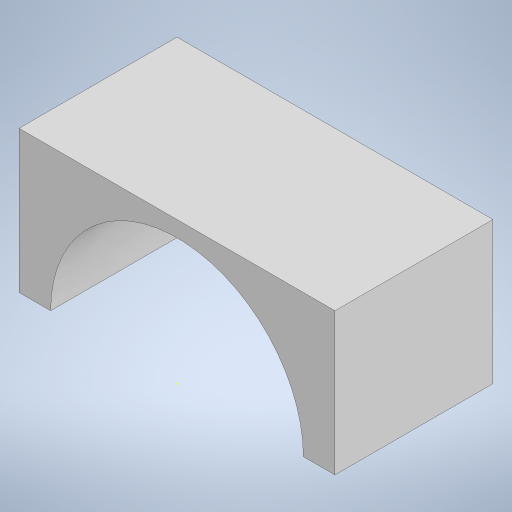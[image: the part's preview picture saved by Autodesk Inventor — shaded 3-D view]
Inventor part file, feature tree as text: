
AUTODESK INVENTOR PART (.ipt)
format: ipt  version: 2023 (Build 270158000, 158)  size: 200,704 bytes
history: native  units: mm
features: sketch x3, extrude x2
ambient origin geometry x8: Origin, YZ Plane, XZ Plane, XY Plane, X Axis, Y Axis, Z Axis, Center Point
bodies: Body1 (feature_tree)
feature tree (5):
  extrude  "Extrusion11"  Depth=45.0mm
  extrude  "Extrusion12"  Depth=50.0mm
  sketch  "Sketch15"  dims[d47=50.0mm d48=0.0mm]
  sketch  "Sketch13"  dims[d42=100.0mm d43=45.0mm]
  sketch  "Sketch14"  dims[d44=50.0mm d45=0.0mm d46=80.0mm]
